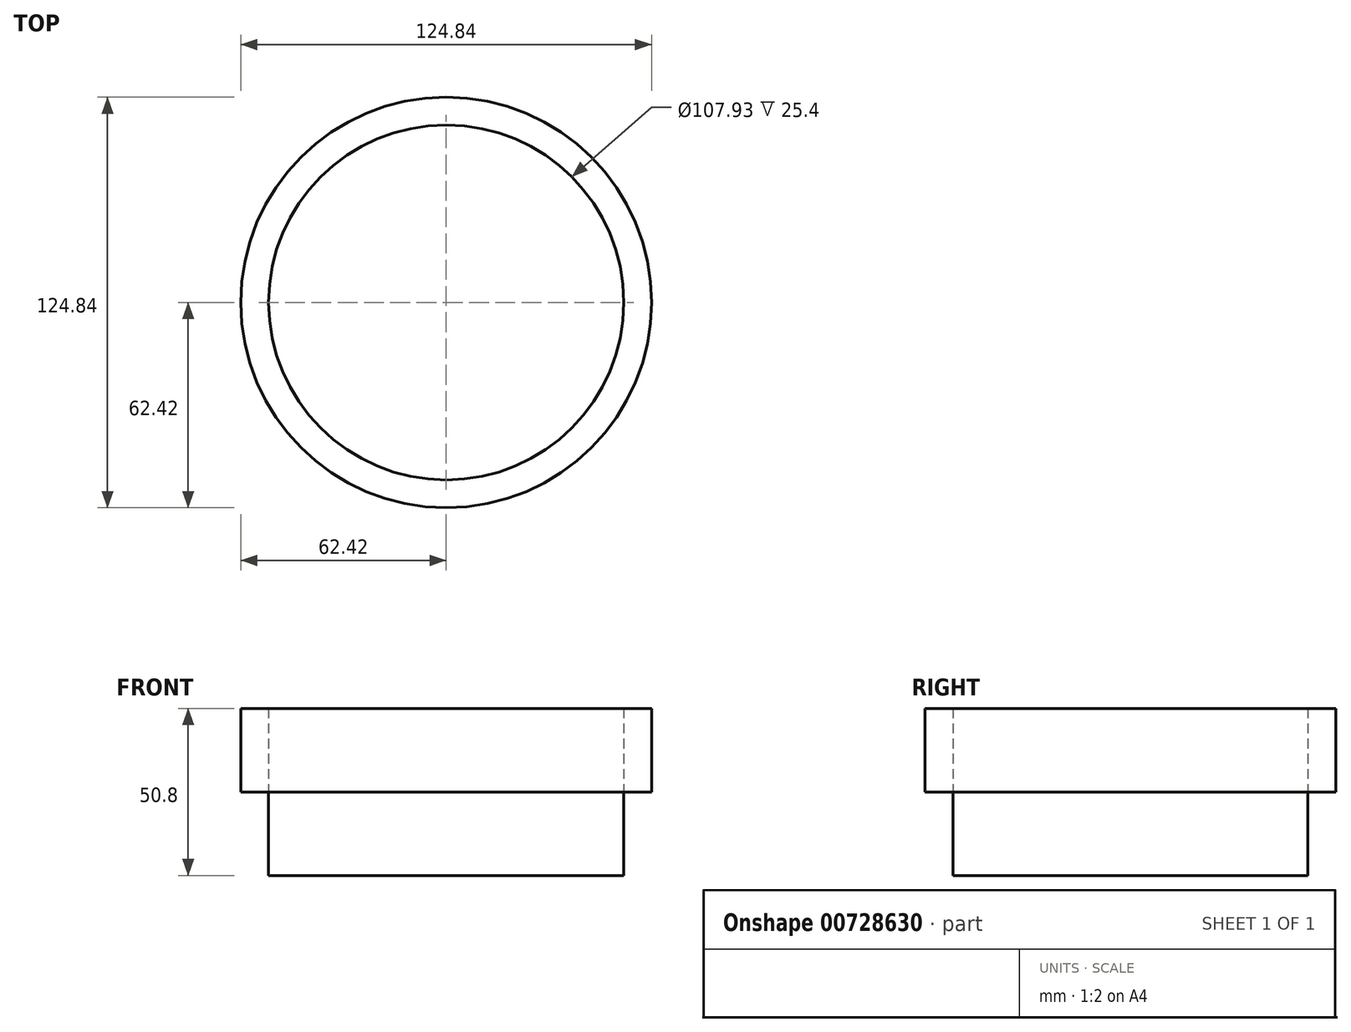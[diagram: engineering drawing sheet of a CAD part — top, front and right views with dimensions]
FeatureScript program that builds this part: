
annotation { "Feature Type Name" : "Feature", "Feature Type Description" : "" }
export const myFeature = defineFeature(function(context is Context, id is Id, definition is map)
    precondition{}
    {
        {
            var Q0;
            Q0=qCreatedBy(makeId("Top.planeOp"),FACE);
            var sketch = newSketch(context, id + "F0", { "sketchPlane" : qUnion([Q0])});
            skCircle(sketch, "E0", {"center": v(0, 0) * mm, "radius": 62.42 * mm});
            skSolve(sketch);
        }
        {
            var Q0;
            Q0=makeQuery(id+"F0.imprint","IMPRINT",FACE,{"disambiguationData":[TD([[makeQuery(id+"F0.imprint","IMPRINT",EDGE,{"derivedFrom":sQuery(id+"F0.wireOp",EDGE,"E0")}),1.0]])]});
            extrude(context, id + "F1", {"entities" : qUnion([Q0]), "depth" : 25.4 * mm, "offsetDistance" : 25.4 * mm});
        }
        {
            var Q0;
            Q0=makeQuery(id+"F1.opExtrude","CAP_FACE",FACE,{"disambiguationData":[OSD([sQuery(id+"F0.wireOp",EDGE,"E0")])],"isStart":false});
            var sketch = newSketch(context, id + "F2", { "sketchPlane" : qUnion([Q0])});
            skCircle(sketch, "E1", {"center": v(0, 0) * mm, "radius": 43.42 * mm});
            skCircle(sketch, "E2", {"center": v(0, 0) * mm, "radius": 53.96 * mm});
            skLineSegment(sketch, "E3", {"start": v(0, 62.42) * mm, "end": v(0, 32.42) * mm, "construction": true});
            skLineSegment(sketch, "E4", {"start": v(0, 32.42) * mm, "end": v(0, 53.96) * mm});
            skLineSegment(sketch, "E5", {"start": v(0, 53.96) * mm, "end": v(3.69, 62.32) * mm});
            skSolve(sketch);
        }
        {
            var Q0;
            Q0=makeQuery(id+"F2.imprint","IMPRINT",FACE,{"disambiguationData":[TD([[makeQuery(id+"F2.imprint","IMPRINT",EDGE,{"derivedFrom":sQuery(id+"F2.wireOp",EDGE,"E2")}),-1.0]])]});
            var sketch = newSketch(context, id + "F3", { "sketchPlane" : qUnion([Q0])});
            skSolve(sketch);
        }
        {
            var Q0;
            Q0=makeQuery(id+"F3.imprint","IMPRINT",FACE,{"disambiguationData":[TD([[makeQuery(id+"F3.imprint","IMPRINT",EDGE,{"derivedFrom":makeQuery(id+"F2.imprint","IMPRINT",EDGE,{"derivedFrom":sQuery(id+"F2.wireOp",EDGE,"E2")})}),-1.0]])]});
            var sketch = newSketch(context, id + "F4", { "sketchPlane" : qUnion([Q0])});
            skSolve(sketch);
        }
        {
            var Q0;
            Q0=makeQuery(id+"F4.imprint","IMPRINT",FACE,{"disambiguationData":[TD([[makeQuery(id+"F4.imprint","IMPRINT",EDGE,{"derivedFrom":makeQuery(id+"F3.imprint","IMPRINT",EDGE,{"derivedFrom":makeQuery(id+"F2.imprint","IMPRINT",EDGE,{"derivedFrom":sQuery(id+"F2.wireOp",EDGE,"E2")})})}),-1.0]])]});
            extrude(context, id + "F5", {"entities" : qUnion([Q0]), "operationType" : NewBodyOperationType.REMOVE, "oppositeDirection" : true, "depth" : 25.4 * mm, "offsetDistance" : 25.4 * mm, "hasSecondDirection" : true, "secondDirectionOppositeDirection" : false, "secondDirectionDepth" : 25.4 * mm});
        }
        {
            var Q0;
            Q0=makeQuery(id+"F3.imprint","IMPRINT",FACE,{"disambiguationData":[TD([[makeQuery(id+"F3.imprint","IMPRINT",EDGE,{"derivedFrom":makeQuery(id+"F2.imprint","IMPRINT",EDGE,{"derivedFrom":sQuery(id+"F2.wireOp",EDGE,"E2")})}),-1.0]])]});
            extrude(context, id + "F6", {"entities" : qUnion([Q0]), "depth" : 25.4 * mm, "offsetDistance" : 25.4 * mm});
        }
    });
